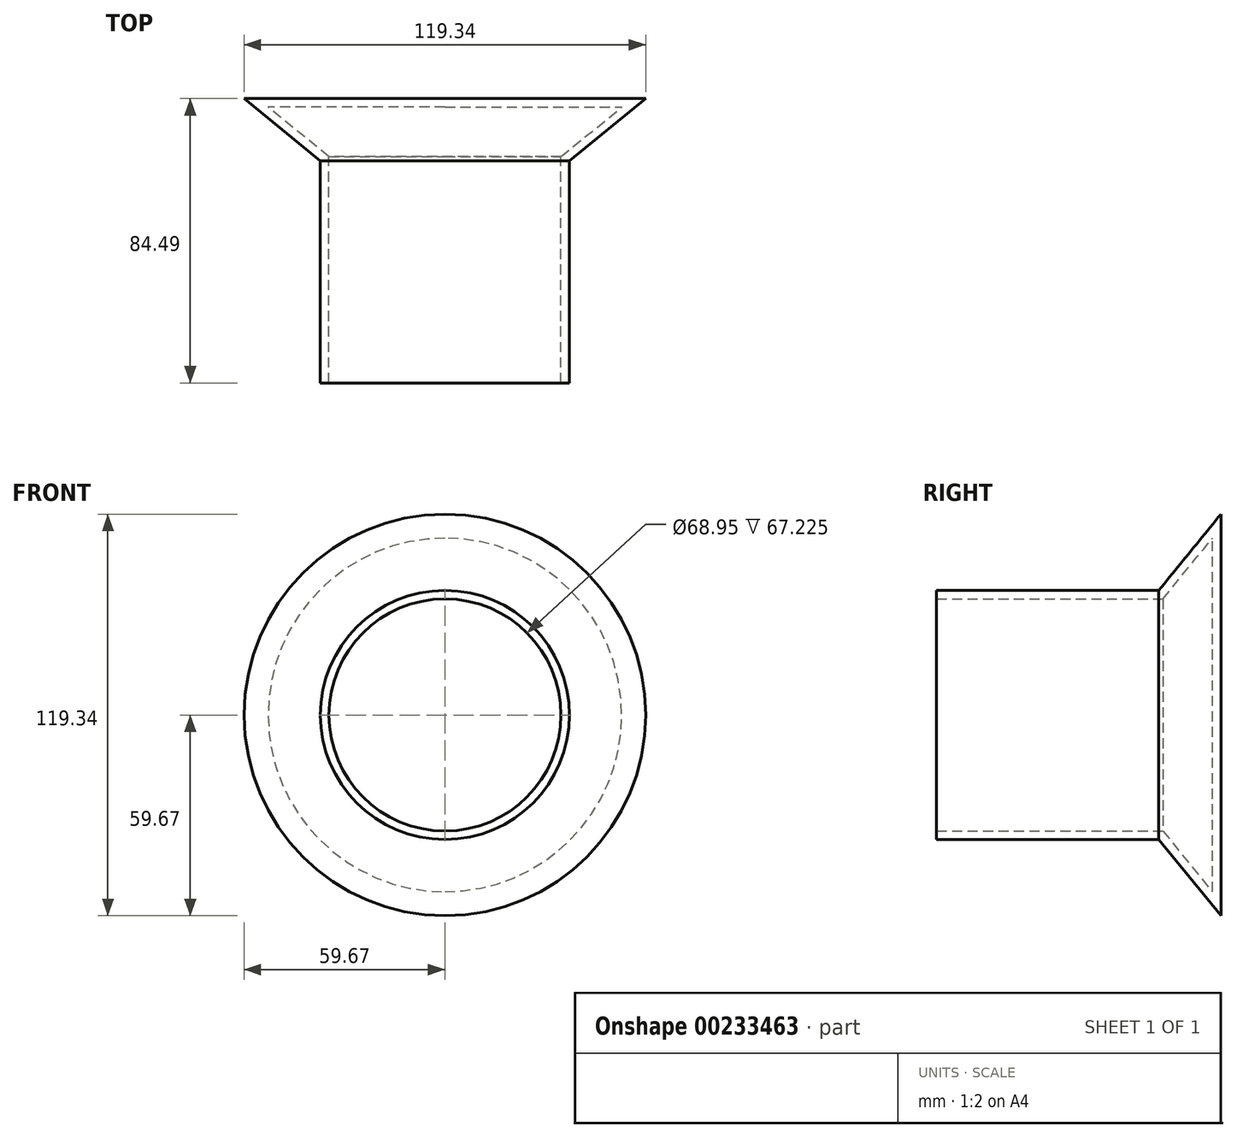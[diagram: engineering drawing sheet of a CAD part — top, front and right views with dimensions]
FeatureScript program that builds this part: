
annotation { "Feature Type Name" : "Feature", "Feature Type Description" : "" }
export const myFeature = defineFeature(function(context is Context, id is Id, definition is map)
    precondition{}
    {
        {
            var Q0;
            Q0=qCreatedBy(makeId("Top.planeOp"),FACE);
            var sketch = newSketch(context, id + "F0", { "sketchPlane" : qUnion([Q0])});
            skLineSegment(sketch, "E0.bottom", {"start": v(0, 0) * mm, "end": v(37.02, 0) * mm});
            skLineSegment(sketch, "E0.top", {"start": v(0, -66.02) * mm, "end": v(37.02, -66.02) * mm});
            skLineSegment(sketch, "E0.left", {"start": v(0, 0) * mm, "end": v(0, -66.02) * mm});
            skLineSegment(sketch, "E0.right", {"start": v(37.02, 0) * mm, "end": v(37.02, -66.02) * mm});
            skLineSegment(sketch, "E1", {"start": v(37.02, 0) * mm, "end": v(59.67, 18.47) * mm});
            skLineSegment(sketch, "E2", {"start": v(59.67, 18.47) * mm, "end": v(0, 18.47) * mm});
            skLineSegment(sketch, "E3", {"start": v(0, 18.47) * mm, "end": v(0, 0) * mm});
            skSolve(sketch);
        }
        {
            var Q0;
            Q0 = qSketchRegion(id + "F0", true);
            var Q1;
            Q1=sQuery(id+"F0.wireOp",EDGE,"E0.left");
            revolve(context, id + "F1", {"entities" : qUnion([Q0]), "axis" : qUnion([Q1]), "revolveType" : RevolveType.FULL});
        }
        {
            var Q0;
            Q0=makeQuery(id+"F1.opRevolve","SWEPT_FACE",FACE,{"disambiguationData":[OSD([sQuery(id+"F0.wireOp",EDGE,"E0.top")])]});
            shell(context, id + "F2", {"entities" : qUnion([Q0]), "thickness" : 2.54 * mm});
        }
    });
